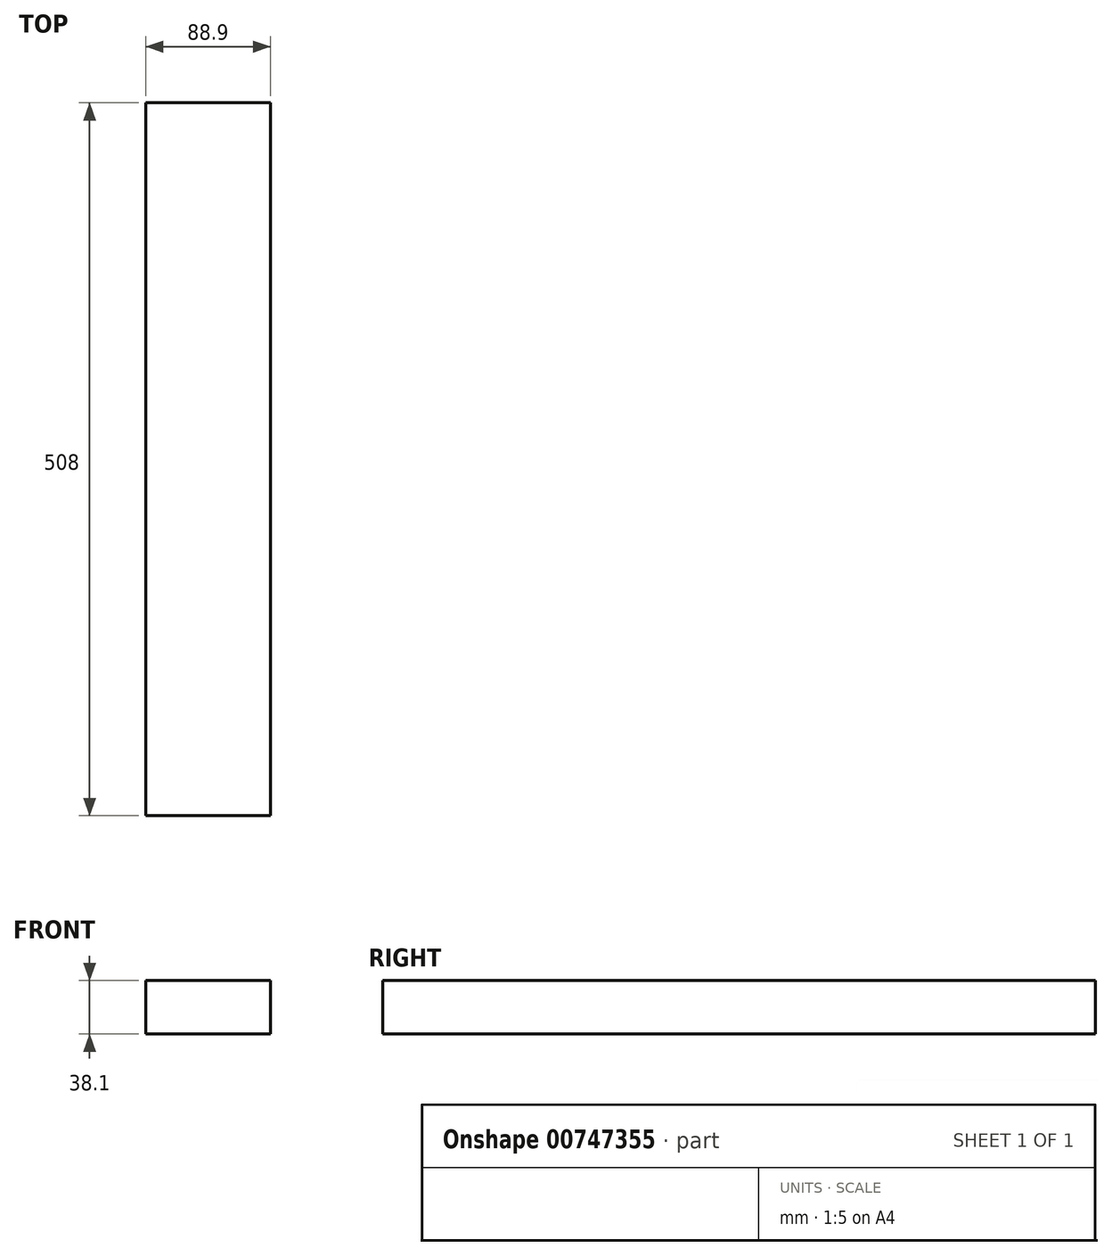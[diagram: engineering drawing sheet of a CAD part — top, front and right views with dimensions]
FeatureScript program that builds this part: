
annotation { "Feature Type Name" : "Feature", "Feature Type Description" : "" }
export const myFeature = defineFeature(function(context is Context, id is Id, definition is map)
    precondition{}
    {
        {
            var Q0;
            Q0=qCreatedBy(makeId("Front.planeOp"),FACE);
            var sketch = newSketch(context, id + "F0", { "sketchPlane" : qUnion([Q0])});
            skLineSegment(sketch, "E0.bottom", {"start": v(0, 0) * mm, "end": v(88.9, 0) * mm});
            skLineSegment(sketch, "E0.top", {"start": v(0, 38.1) * mm, "end": v(88.9, 38.1) * mm});
            skLineSegment(sketch, "E0.left", {"start": v(0, 0) * mm, "end": v(0, 38.1) * mm});
            skLineSegment(sketch, "E0.right", {"start": v(88.9, 0) * mm, "end": v(88.9, 38.1) * mm});
            skSolve(sketch);
        }
        {
            var Q0;
            Q0=qSketchRegion(id+"F0",true);
            extrude(context, id + "F1", {"entities" : qUnion([Q0]), "depth" : 508 * mm, "offsetDistance" : 25.4 * mm});
        }
    });
